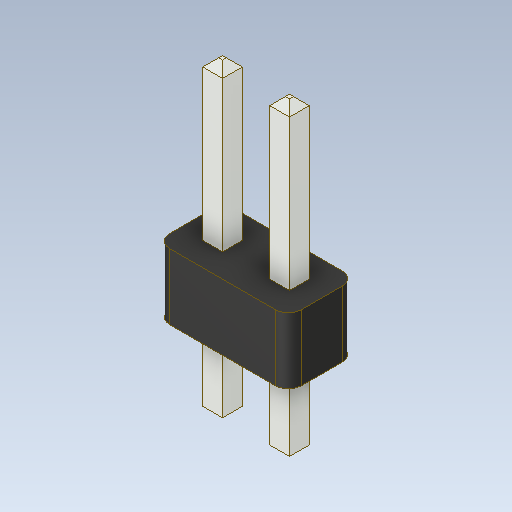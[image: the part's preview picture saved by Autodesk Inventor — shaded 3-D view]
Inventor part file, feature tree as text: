
AUTODESK INVENTOR PART (.ipt)
format: ipt  version: 2020.1 (Build 241239000, 239)  size: 125,440 bytes
history: native  units: mm
features: chamfer x1
ambient origin geometry x8: Origin, YZ Plane, XZ Plane, XY Plane, X Axis, Y Axis, Z Axis, Center Point
bodies: Solid1 (feature_tree)
feature tree (1):
  chamfer  "Chamfer1"  [1 undecoded]
note: 1 required parameter value undecoded (feature->parameter linkage not recoverable at this tier; creation-order binding heuristic only, values carry confidence <= 0.55)
